# Revit family: Accessory-Grab_Bars-KOHLER-Contemporary-K-14561
name_source: partatom
category: Generic Models
revit_build: Autodesk Revit 2015 (Build: 20140606_1530(x64)
units: mm (PartAtom-declared; Revit-internal decimal feet)

## types (4) — shared parameters
ADA Compliant = Yes
Assembly Code = C1030200
Date Modified = 09/15/2017
Default Elevation = 42"
Description = Contemporary 18inch grab bar
Height = 2 3/4"
Length = 20 13/16"
Manufacturer = Kohler
MasterFormat 1995 = 10820
MasterFormat 2004 = 10.28.13
Material = Premium Metal
Product Documentation Link = http://www.us.kohler.com
Product Name = Contemporary
Product Page URL = http://www.us.kohler.com
URL = http://www.us.kohler.com
Width = 2 13/16"

## per-type parameters (varying)
| type | Finish | Model | Type |
| S-Polished Stainless | Metal-Kohler-S-Polished Stainless | K-14561-S | 1 |
| BN-Vibrant Brushed Nickel | Metal-Kohler-BN-Vibrant Brushed Nickel | K-14561-BN | 2 |
| BS-Brushed Stainless | Metal-Kohler-BS-Brushed Stainless | K-14561-BS | 3 |
| TT-Vibrant Titanium | Metal-Kohler-TT-Vibrant Titanium | K-14561-TT | 4 |

## geometry (parser evidence)
native form markers: Sweep x7
no freeform markers — native parametric forms only
